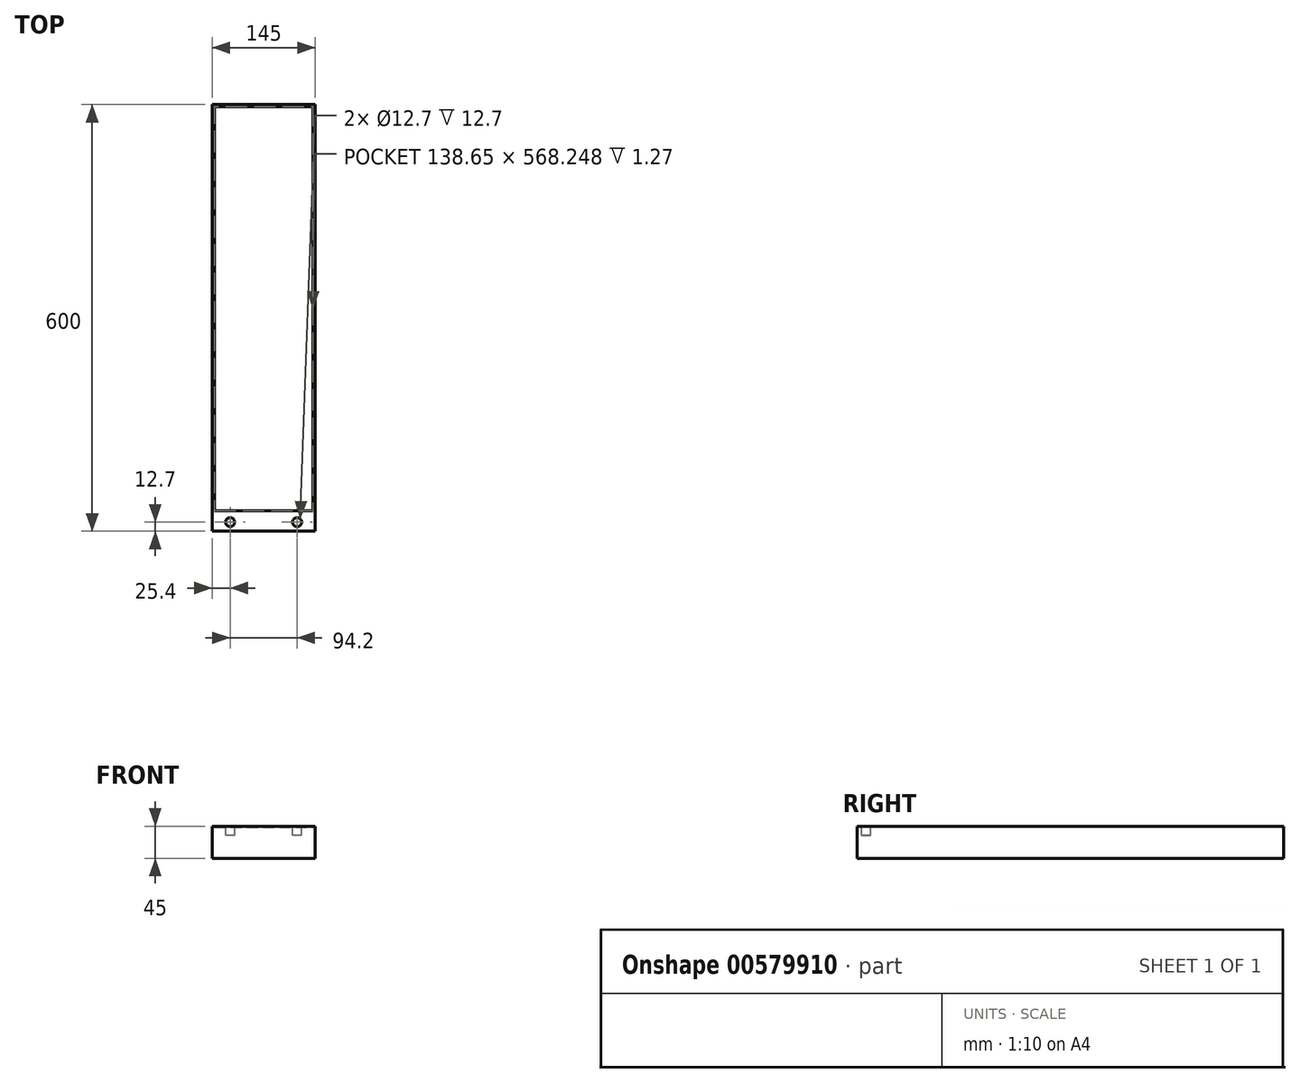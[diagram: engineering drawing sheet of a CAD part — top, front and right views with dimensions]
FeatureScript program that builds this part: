
annotation { "Feature Type Name" : "Feature", "Feature Type Description" : "" }
export const myFeature = defineFeature(function(context is Context, id is Id, definition is map)
    precondition{}
    {
        {
            var Q0;
            Q0=qCreatedBy(makeId("Top.planeOp"),FACE);
            var sketch = newSketch(context, id + "F0", { "sketchPlane" : qUnion([Q0])});
            skLineSegment(sketch, "E0.bottom", {"start": v(0, 0) * mm, "end": v(145, 0) * mm});
            skLineSegment(sketch, "E0.top", {"start": v(0, 600) * mm, "end": v(145, 600) * mm});
            skLineSegment(sketch, "E0.left", {"start": v(0, 0) * mm, "end": v(0, 600) * mm});
            skLineSegment(sketch, "E0.right", {"start": v(145, 0) * mm, "end": v(145, 600) * mm});
            skSolve(sketch);
        }
        {
            var Q0;
            Q0 = qSketchRegion(id + "F0", true);
            extrude(context, id + "F1", {"entities" : qUnion([Q0]), "depth" : 45 * mm, "offsetDistance" : 25.4 * mm});
        }
        {
            var Q0;
            Q0=makeQuery(id+"F1.opExtrude","CAP_FACE",FACE,{"disambiguationData":[OSD([sQuery(id+"F0.wireOp",EDGE,"E0.bottom"),sQuery(id+"F0.wireOp",EDGE,"E0.top"),sQuery(id+"F0.wireOp",EDGE,"E0.left"),sQuery(id+"F0.wireOp",EDGE,"E0.right")])],"isStart":false});
            var sketch = newSketch(context, id + "F2", { "sketchPlane" : qUnion([Q0])});
            skLineSegment(sketch, "E1.bottom", {"start": v(3.17, 596.82) * mm, "end": v(141.82, 596.82) * mm});
            skLineSegment(sketch, "E1.top", {"start": v(3.18, 28.58) * mm, "end": v(141.82, 28.58) * mm});
            skLineSegment(sketch, "E1.left", {"start": v(3.17, 596.82) * mm, "end": v(3.18, 28.58) * mm});
            skLineSegment(sketch, "E1.right", {"start": v(141.82, 596.82) * mm, "end": v(141.82, 28.58) * mm});
            skSolve(sketch);
        }
        {
            var Q0;
            Q0 = qSketchRegion(id + "F2", true);
            extrude(context, id + "F3", {"entities" : qUnion([Q0]), "operationType" : NewBodyOperationType.REMOVE, "oppositeDirection" : true, "depth" : 1.27 * mm, "offsetDistance" : 25.4 * mm});
        }
        {
            var Q0;
            Q0=makeQuery(id+"F1.opExtrude","CAP_FACE",FACE,{"disambiguationData":[OSD([sQuery(id+"F0.wireOp",EDGE,"E0.bottom"),sQuery(id+"F0.wireOp",EDGE,"E0.top"),sQuery(id+"F0.wireOp",EDGE,"E0.left"),sQuery(id+"F0.wireOp",EDGE,"E0.right")])],"isStart":false});
            var sketch = newSketch(context, id + "F4", { "sketchPlane" : qUnion([Q0])});
            skCircle(sketch, "E2", {"center": v(25.4, 12.7) * mm, "radius": 6.35 * mm});
            skCircle(sketch, "E3", {"center": v(119.6, 12.7) * mm, "radius": 6.35 * mm});
            skSolve(sketch);
        }
        {
            var Q0;
            Q0 = qSketchRegion(id + "F4", true);
            extrude(context, id + "F5", {"entities" : qUnion([Q0]), "operationType" : NewBodyOperationType.REMOVE, "oppositeDirection" : true, "depth" : 12.7 * mm, "offsetDistance" : 25.4 * mm});
        }
    });
